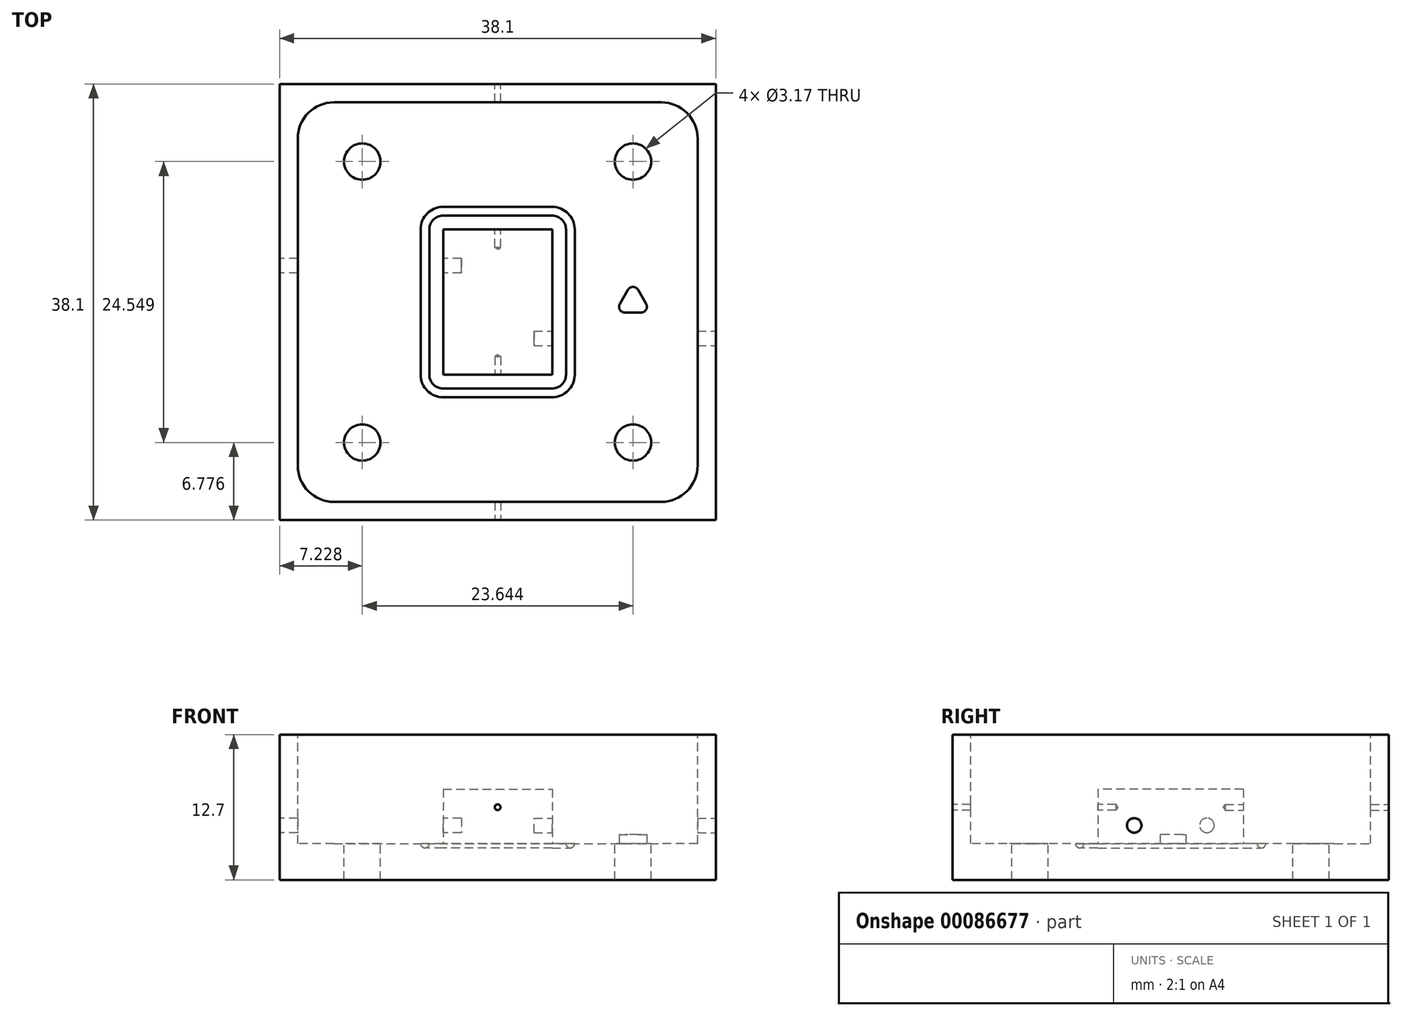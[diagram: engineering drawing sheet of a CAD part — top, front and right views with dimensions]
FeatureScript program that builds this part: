
annotation { "Feature Type Name" : "Feature", "Feature Type Description" : "" }
export const myFeature = defineFeature(function(context is Context, id is Id, definition is map)
    precondition{}
    {
        {
            var Q0;
            Q0=qCreatedBy(makeId("Top.planeOp"),FACE);
            var sketch = newSketch(context, id + "F0", { "sketchPlane" : qUnion([Q0])});
            skLineSegment(sketch, "E0.bottom", {"start": v(-19.05, 19.05) * mm, "end": v(19.05, 19.05) * mm});
            skLineSegment(sketch, "E0.top", {"start": v(-19.05, -19.05) * mm, "end": v(19.05, -19.05) * mm});
            skLineSegment(sketch, "E0.left", {"start": v(-19.05, 19.05) * mm, "end": v(-19.05, -19.05) * mm});
            skLineSegment(sketch, "E0.right", {"start": v(19.05, 19.05) * mm, "end": v(19.05, -19.05) * mm});
            skLineSegment(sketch, "E1", {"start": v(-19.05, 0) * mm, "end": v(19.05, 0) * mm, "construction": true});
            skSolve(sketch);
        }
        {
            var Q0;
            Q0=qSketchRegion(id+"F0",true);
            var Q1;
            Q1=makeQuery(id+"F0.imprint","IMPRINT",FACE,{"disambiguationData":[TD([[makeQuery(id+"F0.imprint","IMPRINT",EDGE,{"derivedFrom":sQuery(id+"F0.wireOp",EDGE,"E0.bottom")}),-1.0]])]});
            extrude(context, id + "F1", {"entities" : qUnion([Q0, Q1]), "depth" : 12.7 * mm});
        }
        {
            var Q0;
            Q0=makeQuery(id+"F1.opExtrude","CAP_FACE",FACE,{"disambiguationData":[OSD([sQuery(id+"F0.wireOp",EDGE,"E0.bottom"),sQuery(id+"F0.wireOp",EDGE,"E0.top"),sQuery(id+"F0.wireOp",EDGE,"E0.left"),sQuery(id+"F0.wireOp",EDGE,"E0.right")])],"isStart":false});
            var sketch = newSketch(context, id + "F2", { "sketchPlane" : qUnion([Q0])});
            skLineSegment(sketch, "E2.bottom", {"start": v(-17.46, 17.46) * mm, "end": v(17.46, 17.46) * mm});
            skLineSegment(sketch, "E2.top", {"start": v(-17.46, -17.46) * mm, "end": v(17.46, -17.46) * mm});
            skLineSegment(sketch, "E2.left", {"start": v(-17.46, 17.46) * mm, "end": v(-17.46, -17.46) * mm});
            skLineSegment(sketch, "E2.right", {"start": v(17.46, 17.46) * mm, "end": v(17.46, -17.46) * mm});
            skLineSegment(sketch, "E3", {"start": v(-17.46, 0) * mm, "end": v(17.46, 0) * mm, "construction": true});
            skSolve(sketch);
        }
        {
            var Q0;
            Q0=qSketchRegion(id+"F2",true);
            extrude(context, id + "F3", {"entities" : qUnion([Q0]), "operationType" : NewBodyOperationType.REMOVE, "oppositeDirection" : true, "depth" : 9.52 * mm});
        }
        {
            var Q0;
            Q0=makeQuery(id+"F3.boolean.opBoolean","COPY",FACE,{"derivedFrom":makeQuery(id+"F3.opExtrude","CAP_FACE",FACE,{"disambiguationData":[OSD([sQuery(id+"F2.wireOp",EDGE,"E2.bottom"),sQuery(id+"F2.wireOp",EDGE,"E2.top"),sQuery(id+"F2.wireOp",EDGE,"E2.left"),sQuery(id+"F2.wireOp",EDGE,"E2.right")])],"isStart":false})});
            var sketch = newSketch(context, id + "F4", { "sketchPlane" : qUnion([Q0])});
            skLineSegment(sketch, "E4.bottom", {"start": v(-4.76, 6.35) * mm, "end": v(4.76, 6.35) * mm});
            skLineSegment(sketch, "E4.top", {"start": v(-4.76, -6.35) * mm, "end": v(4.76, -6.35) * mm});
            skLineSegment(sketch, "E4.left", {"start": v(-4.76, 6.35) * mm, "end": v(-4.76, -6.35) * mm});
            skLineSegment(sketch, "E4.right", {"start": v(4.76, 6.35) * mm, "end": v(4.76, -6.35) * mm});
            skLineSegment(sketch, "E5", {"start": v(-4.76, 0) * mm, "end": v(4.76, 0) * mm, "construction": true});
            skSolve(sketch);
        }
        {
            var Q0;
            Q0=qSketchRegion(id+"F4",true);
            extrude(context, id + "F5", {"entities" : qUnion([Q0]), "operationType" : NewBodyOperationType.ADD, "depth" : 4.76 * mm});
        }
        {
            var Q0;
            Q0=makeQuery(id+"F1.opExtrude","SWEPT_FACE",FACE,{"disambiguationData":[OSD([sQuery(id+"F0.wireOp",EDGE,"E0.top")])]});
            var sketch = newSketch(context, id + "F6", { "sketchPlane" : qUnion([Q0])});
            skLineSegment(sketch, "E6", {"start": v(0, 12.7) * mm, "end": v(0, 6.35) * mm, "construction": true});
            skPoint(sketch, "E6.endSnap0", {"position": v(0, 12.7) * mm});
            skSolve(sketch);
        }
        {
            var Q0;
            Q0=sQuery(id+"F6.wireOp",VERTEX,"E6.end");
            var Q1;
            Q1=makeQuery(id+"F1.opExtrude","SWEPT_BODY",BODY,{"disambiguationData":[OSD([sQuery(id+"F0.wireOp",EDGE,"E0.bottom"),sQuery(id+"F0.wireOp",EDGE,"E0.top"),sQuery(id+"F0.wireOp",EDGE,"E0.left"),sQuery(id+"F0.wireOp",EDGE,"E0.right")])]});
            hole(context, id + "F7", {"style" : HoleStyle.SIMPLE, "endStyle" : HoleEndStyle.BLIND, "holeDiameter" : 0.5 * mm, "holeDepth" : 14.29 * mm, "locations" : qUnion([Q0]), "scope" : qUnion([Q1])});
        }
        {
            var Q0;
            Q0=makeQuery(id+"F1.opExtrude","SWEPT_FACE",FACE,{"disambiguationData":[OSD([sQuery(id+"F0.wireOp",EDGE,"E0.bottom")])]});
            var sketch = newSketch(context, id + "F8", { "sketchPlane" : qUnion([Q0])});
            skLineSegment(sketch, "E7", {"start": v(0, 12.7) * mm, "end": v(0, 6.35) * mm, "construction": true});
            skPoint(sketch, "E7.endSnap0", {"position": v(0, 12.7) * mm});
            skSolve(sketch);
        }
        {
            var Q0;
            Q0=sQuery(id+"F8.wireOp",VERTEX,"E7.end");
            var Q1;
            Q1=makeQuery(id+"F1.opExtrude","SWEPT_BODY",BODY,{"disambiguationData":[OSD([sQuery(id+"F0.wireOp",EDGE,"E0.bottom"),sQuery(id+"F0.wireOp",EDGE,"E0.top"),sQuery(id+"F0.wireOp",EDGE,"E0.left"),sQuery(id+"F0.wireOp",EDGE,"E0.right")])]});
            hole(context, id + "F9", {"style" : HoleStyle.SIMPLE, "endStyle" : HoleEndStyle.BLIND, "holeDiameter" : 0.5 * mm, "holeDepth" : 14.29 * mm, "locations" : qUnion([Q0]), "scope" : qUnion([Q1])});
        }
        {
            var Q0;
            Q0=makeQuery(id+"F3.boolean.opBoolean","COPY",EDGE,{"derivedFrom":makeQuery(id+"F3.opExtrude","SWEPT_EDGE",EDGE,{"disambiguationData":[OSD([sQuery(id+"F2.wireOp",EDGE,"E2.bottom"),sQuery(id+"F2.wireOp",EDGE,"E2.left")])]})});
            var Q1;
            Q1=makeQuery(id+"F3.boolean.opBoolean","COPY",EDGE,{"derivedFrom":makeQuery(id+"F3.opExtrude","SWEPT_EDGE",EDGE,{"disambiguationData":[OSD([sQuery(id+"F2.wireOp",EDGE,"E2.top"),sQuery(id+"F2.wireOp",EDGE,"E2.left")])]})});
            var Q2;
            Q2=makeQuery(id+"F3.boolean.opBoolean","COPY",EDGE,{"derivedFrom":makeQuery(id+"F3.opExtrude","SWEPT_EDGE",EDGE,{"disambiguationData":[OSD([sQuery(id+"F2.wireOp",EDGE,"E2.top"),sQuery(id+"F2.wireOp",EDGE,"E2.right")])]})});
            var Q3;
            Q3=makeQuery(id+"F3.boolean.opBoolean","COPY",EDGE,{"derivedFrom":makeQuery(id+"F3.opExtrude","SWEPT_EDGE",EDGE,{"disambiguationData":[OSD([sQuery(id+"F2.wireOp",EDGE,"E2.bottom"),sQuery(id+"F2.wireOp",EDGE,"E2.right")])]})});
            fillet(context, id + "F10", {"entities" : qUnion([Q0, Q1, Q2, Q3]), "radius" : 3.17 * mm, "tangentPropagation" : true, "allowEdgeOverflow" : false});
        }
        {
            var Q0;
            Q0=makeQuery(id+"F3.boolean.opBoolean","COPY",FACE,{"derivedFrom":makeQuery(id+"F3.opExtrude","CAP_FACE",FACE,{"disambiguationData":[OSD([sQuery(id+"F2.wireOp",EDGE,"E2.bottom"),sQuery(id+"F2.wireOp",EDGE,"E2.top"),sQuery(id+"F2.wireOp",EDGE,"E2.left"),sQuery(id+"F2.wireOp",EDGE,"E2.right")])],"isStart":false})});
            var sketch = newSketch(context, id + "F11", { "sketchPlane" : qUnion([Q0])});
            skLineSegment(sketch, "E8.bottom", {"start": v(4.76, -7.94) * mm, "end": v(-4.76, -7.94) * mm});
            skLineSegment(sketch, "E8.top", {"start": v(4.76, 7.94) * mm, "end": v(-4.76, 7.94) * mm});
            skLineSegment(sketch, "E8.left", {"start": v(6.35, -6.35) * mm, "end": v(6.35, 6.35) * mm});
            skPoint(sketch, "E8.middle", {"position": v(0, 0) * mm});
            skPoint(sketch, "E9.visualSharp", {"position": v(-6.35, -7.94) * mm});
            skArc(sketch, "E9.filletArc", {"start": v(-6.35, -6.35) * mm, "mid": v(-5.89, -7.47) * mm, "end": v(-4.76, -7.94) * mm});
            skPoint(sketch, "E10.visualSharp", {"position": v(-6.35, 7.94) * mm});
            skArc(sketch, "E10.filletArc", {"start": v(-4.76, 7.94) * mm, "mid": v(-5.89, 7.47) * mm, "end": v(-6.35, 6.35) * mm});
            skPoint(sketch, "E11.visualSharp", {"position": v(6.35, -7.94) * mm});
            skArc(sketch, "E11.filletArc", {"start": v(4.76, -7.94) * mm, "mid": v(5.89, -7.47) * mm, "end": v(6.35, -6.35) * mm});
            skPoint(sketch, "E12.visualSharp", {"position": v(6.35, 7.94) * mm});
            skArc(sketch, "E12.filletArc", {"start": v(6.35, 6.35) * mm, "mid": v(5.89, 7.47) * mm, "end": v(4.76, 7.94) * mm});
            skLineSegment(sketch, "E13", {"start": v(-6.35, 6.35) * mm, "end": v(-6.35, 0) * mm});
            skLineSegment(sketch, "E14", {"start": v(-6.35, 0) * mm, "end": v(-6.35, -6.35) * mm});
            skSolve(sketch);
        }
        {
            var Q0;
            Q0=qCreatedBy(makeId("Front.planeOp"),FACE);
            var sketch = newSketch(context, id + "F12", { "sketchPlane" : qUnion([Q0])});
            skArc(sketch, "E15", {"start": v(-6.73, 3.17) * mm, "mid": v(-6.35, 2.8) * mm, "end": v(-5.97, 3.17) * mm});
            skLineSegment(sketch, "E16", {"start": v(-6.73, 3.17) * mm, "end": v(-5.97, 3.17) * mm});
            skSolve(sketch);
        }
        {
            var Q0;
            Q0=qSketchRegion(id+"F12",true);
            var Q1;
            Q1=qConstructionFilter(qBodyType(qCreatedBy(id+"F11",EDGE),BodyType.WIRE),ConstructionObject.NO);
            sweep(context, id + "F13", {"operationType" : NewBodyOperationType.REMOVE, "profiles" : qUnion([Q0]), "path" : qUnion([Q1])});
        }
        {
            var Q0;
            {var subQ1=sQuery(id+"F2.wireOp",EDGE,"E2.right");var subQ2=sQuery(id+"F2.wireOp",EDGE,"E2.bottom");var subQ3=sQuery(id+"F2.wireOp",EDGE,"E2.top");var subQ4=sQuery(id+"F2.wireOp",EDGE,"E2.left");Q0=makeQuery(id+"F13.boolean.opBoolean","SPLIT",FACE,{"disambiguationData":[TD([makeQuery(id+"F3.boolean.opBoolean","COPY",FACE,{"derivedFrom":makeQuery(id+"F3.opExtrude","SWEPT_FACE",FACE,{"disambiguationData":[OSD([subQ2])]})})])],"derivedFrom":makeQuery(id+"F3.boolean.opBoolean","COPY",FACE,{"derivedFrom":makeQuery(id+"F3.opExtrude","CAP_FACE",FACE,{"disambiguationData":[OSD([subQ2,subQ3,subQ4,subQ1])],"isStart":false})})});}
            var sketch = newSketch(context, id + "F14", { "sketchPlane" : qUnion([Q0])});
            skLineSegment(sketch, "E17", {"start": v(-16.53, 16.53) * mm, "end": v(-11.82, 12.27) * mm, "construction": true});
            skLineSegment(sketch, "E18", {"start": v(16.53, 16.53) * mm, "end": v(11.82, 12.27) * mm, "construction": true});
            skLineSegment(sketch, "E19", {"start": v(-16.53, -16.53) * mm, "end": v(-11.82, -12.27) * mm, "construction": true});
            skLineSegment(sketch, "E20", {"start": v(16.53, -16.53) * mm, "end": v(11.82, -12.27) * mm, "construction": true});
            skSolve(sketch);
        }
        {
            var Q0;
            Q0=sQuery(id+"F14.wireOp",VERTEX,"E20.end");
            var Q1;
            Q1=sQuery(id+"F14.wireOp",VERTEX,"E18.end");
            var Q2;
            Q2=sQuery(id+"F14.wireOp",VERTEX,"E17.end");
            var Q3;
            Q3=sQuery(id+"F14.wireOp",VERTEX,"E19.end");
            var Q4;
            Q4=makeQuery(id+"F1.opExtrude","SWEPT_BODY",BODY,{"disambiguationData":[OSD([sQuery(id+"F0.wireOp",EDGE,"E0.bottom"),sQuery(id+"F0.wireOp",EDGE,"E0.top"),sQuery(id+"F0.wireOp",EDGE,"E0.left"),sQuery(id+"F0.wireOp",EDGE,"E0.right")])]});
            hole(context, id + "F15", {"style" : HoleStyle.SIMPLE, "endStyle" : HoleEndStyle.THROUGH, "holeDiameter" : 3.17 * mm, "locations" : qUnion([Q0, Q1, Q2, Q3]), "scope" : qUnion([Q4]), "isTappedThrough" : true});
        }
        {
            var Q0;
            {var subQ1=sQuery(id+"F2.wireOp",EDGE,"E2.right");var subQ2=sQuery(id+"F2.wireOp",EDGE,"E2.bottom");var subQ3=sQuery(id+"F2.wireOp",EDGE,"E2.top");var subQ4=sQuery(id+"F2.wireOp",EDGE,"E2.left");Q0=makeQuery(id+"F13.boolean.opBoolean","SPLIT",FACE,{"disambiguationData":[TD([makeQuery(id+"F3.boolean.opBoolean","COPY",FACE,{"derivedFrom":makeQuery(id+"F3.opExtrude","SWEPT_FACE",FACE,{"disambiguationData":[OSD([subQ2])]})})])],"derivedFrom":makeQuery(id+"F3.boolean.opBoolean","COPY",FACE,{"derivedFrom":makeQuery(id+"F3.opExtrude","CAP_FACE",FACE,{"disambiguationData":[OSD([subQ2,subQ3,subQ4,subQ1])],"isStart":false})})});}
            var sketch = newSketch(context, id + "F16", { "sketchPlane" : qUnion([Q0])});
            skLineSegment(sketch, "E21", {"start": v(11.82, 12.27) * mm, "end": v(11.82, -12.27) * mm, "construction": true});
            skLineSegment(sketch, "E22", {"start": v(11.82, -12.27) * mm, "end": v(11.82, 0) * mm, "construction": true});
            skCircle(sketch, "E23.cCircle", {"center": v(11.82, 0) * mm, "radius": 0.92 * mm, "construction": true});
            skLineSegment(sketch, "E23.0", {"start": v(13.4, -0.92) * mm, "end": v(10.23, -0.92) * mm});
            skLineSegment(sketch, "E23.1", {"start": v(10.23, -0.92) * mm, "end": v(11.82, 1.83) * mm});
            skLineSegment(sketch, "E23.2", {"start": v(11.82, 1.83) * mm, "end": v(13.4, -0.92) * mm});
            skPoint(sketch, "E23.0.midPoint", {"position": v(11.82, -0.92) * mm});
            skSolve(sketch);
        }
        {
            var Q0;
            Q0=makeQuery(id+"F16.imprint","IMPRINT",FACE,{"disambiguationData":[TD([[makeQuery(id+"F16.imprint","IMPRINT",EDGE,{"derivedFrom":sQuery(id+"F16.wireOp",EDGE,"E23.0")}),-1.0]])]});
            extrude(context, id + "F17", {"entities" : qUnion([Q0]), "operationType" : NewBodyOperationType.ADD, "depth" : 0.8 * mm});
        }
        {
            var Q0;
            Q0=makeQuery(id+"F17.opExtrude","SWEPT_EDGE",EDGE,{"disambiguationData":[OSD([sQuery(id+"F16.wireOp",EDGE,"E23.1"),sQuery(id+"F16.wireOp",EDGE,"E23.2")])]});
            var Q1;
            Q1=makeQuery(id+"F17.opExtrude","SWEPT_EDGE",EDGE,{"disambiguationData":[OSD([sQuery(id+"F16.wireOp",EDGE,"E23.0"),sQuery(id+"F16.wireOp",EDGE,"E23.2")])]});
            var Q2;
            Q2=makeQuery(id+"F17.opExtrude","SWEPT_EDGE",EDGE,{"disambiguationData":[OSD([sQuery(id+"F16.wireOp",EDGE,"E23.0"),sQuery(id+"F16.wireOp",EDGE,"E23.1")])]});
            fillet(context, id + "F18", {"entities" : qUnion([Q0, Q1, Q2]), "radius" : 0.5 * mm, "tangentPropagation" : true, "allowEdgeOverflow" : false});
        }
        {
            var Q0;
            Q0=makeQuery(id+"F1.opExtrude","SWEPT_FACE",FACE,{"disambiguationData":[OSD([sQuery(id+"F0.wireOp",EDGE,"E0.right")])]});
            var sketch = newSketch(context, id + "F19", { "sketchPlane" : qUnion([Q0])});
            skLineSegment(sketch, "E24.bottom", {"start": v(-19.05, 0) * mm, "end": v(-3.17, 0) * mm, "construction": true});
            skLineSegment(sketch, "E24.top", {"start": v(-19.05, 4.76) * mm, "end": v(-3.17, 4.76) * mm, "construction": true});
            skLineSegment(sketch, "E24.left", {"start": v(-19.05, 0) * mm, "end": v(-19.05, 4.76) * mm, "construction": true});
            skLineSegment(sketch, "E24.right", {"start": v(-3.17, 0) * mm, "end": v(-3.17, 4.76) * mm, "construction": true});
            skCircle(sketch, "E25", {"center": v(-3.17, 4.76) * mm, "radius": 0.64 * mm});
            skSolve(sketch);
        }
        {
            var Q0;
            Q0=makeQuery(id+"F19.imprint","IMPRINT",FACE,{"disambiguationData":[TD([[makeQuery(id+"F19.imprint","IMPRINT",EDGE,{"derivedFrom":sQuery(id+"F19.wireOp",EDGE,"E25")}),1.0]])]});
            extrude(context, id + "F20", {"entities" : qUnion([Q0]), "operationType" : NewBodyOperationType.REMOVE, "oppositeDirection" : true, "depth" : 15.88 * mm});
        }
        {
            var Q0;
            Q0=makeQuery(id+"F1.opExtrude","SWEPT_FACE",FACE,{"disambiguationData":[OSD([sQuery(id+"F0.wireOp",EDGE,"E0.left")])]});
            var sketch = newSketch(context, id + "F21", { "sketchPlane" : qUnion([Q0])});
            skLineSegment(sketch, "E26.bottom", {"start": v(-19.05, 0) * mm, "end": v(-3.17, 0) * mm, "construction": true});
            skLineSegment(sketch, "E26.top", {"start": v(-19.05, 4.76) * mm, "end": v(-3.17, 4.76) * mm, "construction": true});
            skLineSegment(sketch, "E26.left", {"start": v(-19.05, 0) * mm, "end": v(-19.05, 4.76) * mm, "construction": true});
            skLineSegment(sketch, "E26.right", {"start": v(-3.17, 0) * mm, "end": v(-3.17, 4.76) * mm, "construction": true});
            skCircle(sketch, "E27", {"center": v(-3.17, 4.76) * mm, "radius": 0.64 * mm});
            skSolve(sketch);
        }
        {
            var Q0;
            Q0=makeQuery(id+"F21.imprint","IMPRINT",FACE,{"disambiguationData":[TD([[makeQuery(id+"F21.imprint","IMPRINT",EDGE,{"derivedFrom":sQuery(id+"F21.wireOp",EDGE,"E27")}),1.0]])]});
            extrude(context, id + "F22", {"entities" : qUnion([Q0]), "operationType" : NewBodyOperationType.REMOVE, "oppositeDirection" : true, "depth" : 15.88 * mm});
        }
    });
